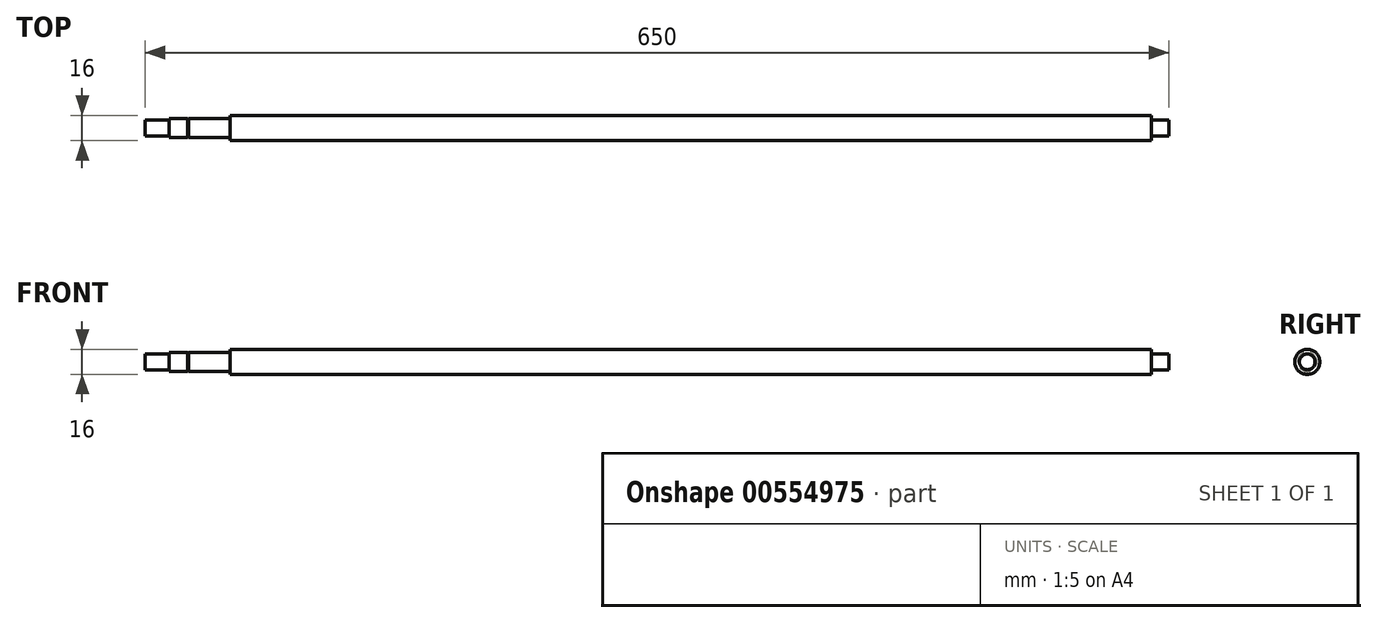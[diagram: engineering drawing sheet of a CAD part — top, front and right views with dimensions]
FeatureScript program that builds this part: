
annotation { "Feature Type Name" : "Feature", "Feature Type Description" : "" }
export const myFeature = defineFeature(function(context is Context, id is Id, definition is map)
    precondition{}
    {
        {
            var Q0;
            Q0=qCreatedBy(makeId("Front.planeOp"),FACE);
            var sketch = newSketch(context, id + "F0", { "sketchPlane" : qUnion([Q0])});
            skLineSegment(sketch, "E0.bottom", {"start": v(-292.5, 0) * mm, "end": v(292.5, 0) * mm});
            skLineSegment(sketch, "E0.top", {"start": v(-292.5, 8) * mm, "end": v(292.5, 8) * mm});
            skLineSegment(sketch, "E0.left", {"start": v(-292.5, 6) * mm, "end": v(-292.5, 8) * mm});
            skLineSegment(sketch, "E0.right", {"start": v(292.5, 5) * mm, "end": v(292.5, 8) * mm});
            skLineSegment(sketch, "E1.top", {"start": v(59.48, 0) * mm, "end": v(292.5, 0) * mm});
            skLineSegment(sketch, "E2.bottom", {"start": v(-292.5, 6) * mm, "end": v(-319, 6) * mm});
            skLineSegment(sketch, "E2.top", {"start": v(-292.5, 0) * mm, "end": v(-331.5, 0) * mm});
            skLineSegment(sketch, "E2.right", {"start": v(-331.5, 6) * mm, "end": v(-331.5, 5) * mm});
            skLineSegment(sketch, "E3.bottom", {"start": v(-331.5, 5) * mm, "end": v(-346.5, 5) * mm});
            skLineSegment(sketch, "E3.top", {"start": v(-331.5, 0) * mm, "end": v(-346.5, 0) * mm});
            skLineSegment(sketch, "E3.right", {"start": v(-346.5, 5) * mm, "end": v(-346.5, 0) * mm});
            skLineSegment(sketch, "E4.bottom", {"start": v(292.5, 5) * mm, "end": v(303.5, 5) * mm});
            skLineSegment(sketch, "E4.top", {"start": v(292.5, 0) * mm, "end": v(303.5, 0) * mm});
            skLineSegment(sketch, "E4.right", {"start": v(303.5, 5) * mm, "end": v(303.5, 0) * mm});
            skLineSegment(sketch, "E5", {"start": v(-319.5, 6) * mm, "end": v(-319.5, 5.5) * mm});
            skLineSegment(sketch, "E6", {"start": v(-319.5, 5.5) * mm, "end": v(-319, 5.5) * mm});
            skLineSegment(sketch, "E7", {"start": v(-319, 5.5) * mm, "end": v(-319, 6) * mm});
            skLineSegment(sketch, "E8.trimOffspring", {"start": v(-319.5, 6) * mm, "end": v(-331.5, 6) * mm});
            skSolve(sketch);
        }
        {
            var Q0;
            Q0 = qSketchRegion(id + "F0", true);
            var Q1;
            Q1=sQuery(id+"F0.wireOp",EDGE,"E0.bottom");
            revolve(context, id + "F1", {"entities" : qUnion([Q0]), "axis" : qUnion([Q1]), "revolveType" : RevolveType.FULL});
        }
    });
